# Revit family: Furniture_Sofas-Armchairs_Fritz-Hansen_Alphabet-SofaT-Series-PL300-3
name_source: partatom
category: Generic Models
revit_build: Autodesk Revit 2017 (Build: 20190508_0315(x64)
units: mm (PartAtom-declared; Revit-internal decimal feet)

## family parameters
Always vertical = No
Can host rebar = No
Cut with Voids When Loaded = No
Part Type = Normal
Room Calculation Point = No
Round Connector Dimension = Use Diameter
Shared = No
Work Plane-Based = No

## types (1)
- Default
    BIMobject category = Sofas & Armchairs
    BIMobject category code = sofas-armchairs
    BIMobject main category = Furniture
    BIMobject main category code = furniture
    Brand url = https://fritzhansen.com
    Design country = Denmark
    Edition number = 1
    Manufacturer country = Denmark
    Manufacturer name = Fritz Hansen
    Material main = Upholstery
    Material secondary = Firm Foam
    Product Guid = 9eade0f3-742d-4a9e-9973-bb54045ca837
    Product SKU = PL300-3
    Product data url = https://bimobject.com
    Product family = Furniture
    Product group = Sofas
    Product name = Alphabet Sofa™ Series PL300-3
    Product url = https://fritzhansen.com
    QR code = http://bimobject.com

## geometry (parser evidence)
native form markers: Sweep x2
no freeform markers — native parametric forms only
